# Revit family: NLRS_33_GM_FB_TC_STORAX_vloerluik_BV-THERMO_BCB
name_source: partatom
category: Generic Models
revit_build: Autodesk Revit 2014 (Build: 20130308_1515(x64)
units: mm (PartAtom-declared; Revit-internal decimal feet)

## types (7) — shared parameters
Default Elevation = 1219 mm
Manufacturer = Storax
Model = BV
RC-waarde = 3.2 m2 K/W
URL = http://www.storax.nl
belasting = 125 kN
binnenluik = tbv betonvulling
brandwerend 90 min = nee
gasdrukveer = nee
geïsoleerd = ja
materiaal = bcb_staal
productgroep = Vloerluiken
rubberen_afdichting = enkel
scharnierend = nee
sluiting = 4
vergrendeling = nee
vullen_met_beton = ja

## per-type parameters (varying)
| type | binnenmaat_breedte | binnenmaat_lengte | gewicht | uitwendige_breedte | uitwendige_lengte |
| BV-THERMO 55 | 500 mm  [stored 1.64042 ft] | 500 mm  [stored 1.64042 ft] | 19 | 635 mm  [stored 2.08333 ft] | 635 mm  [stored 2.08333 ft] |
| BV-THERMO 66 | 600 mm | 600 mm | 23 | 735 mm | 735 mm |
| BV-THERMO 86 | 600 mm | 800 mm | 29 | 735 mm | 935 mm |
| BV-THERMO 88 | 800 mm | 800 mm | 33 | 935 mm | 935 mm |
| BV-THERMO 106 | 600 mm | 1000 mm  [stored 3.28084 ft] | 33 | 735 mm | 1135 mm |
| BV-THERMO 110 | 1000 mm  [stored 3.28084 ft] | 1000 mm  [stored 3.28084 ft] | 45 | 1135 mm | 1135 mm |
| maatwerk | 1000 mm  [stored 3.28084 ft] | 1000 mm  [stored 3.28084 ft] | 45 | 1135 mm | 1135 mm |

note: [stored X ft] marks values corroborated as IEEE doubles in the binary element streams (Revit-internal decimal feet)

## geometry (parser evidence)
native form markers: Blend x819, Sweep x4
no freeform markers — native parametric forms only
